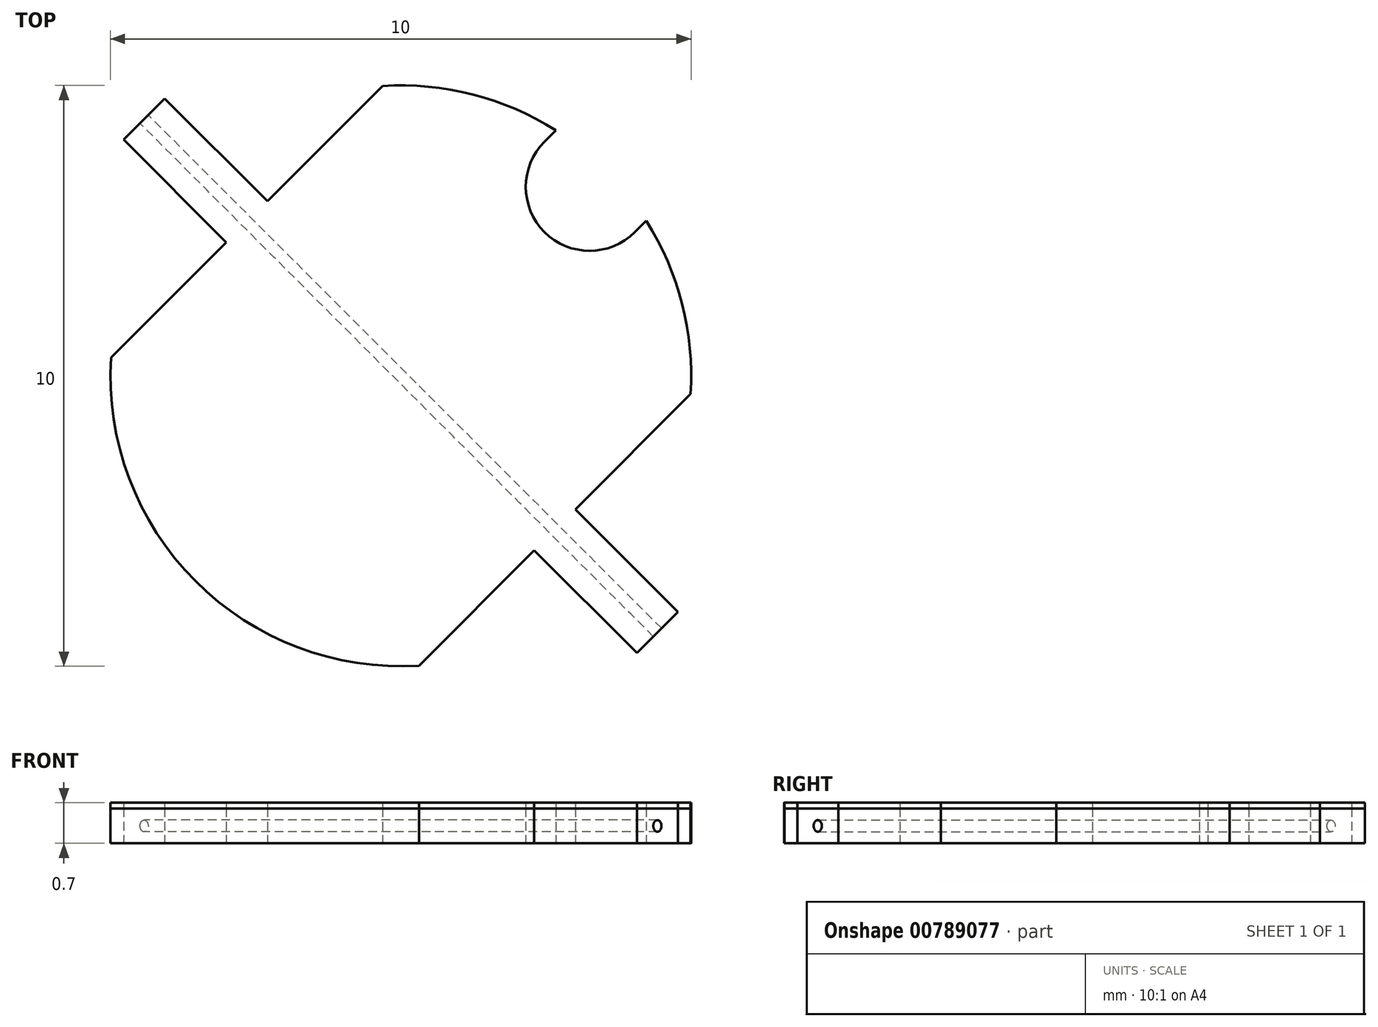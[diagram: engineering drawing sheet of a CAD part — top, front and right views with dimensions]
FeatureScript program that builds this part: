
annotation { "Feature Type Name" : "Feature", "Feature Type Description" : "" }
export const myFeature = defineFeature(function(context is Context, id is Id, definition is map)
    precondition{}
    {
        {
            var Q0;
            Q0=qCreatedBy(makeId("Top.planeOp"),FACE);
            var sketch = newSketch(context, id + "F0", { "sketchPlane" : qUnion([Q0])});
            skArc(sketch, "E0", {"start": v(-5, 0.31) * mm, "mid": v(-3.54, -3.54) * mm, "end": v(0.31, -5) * mm});
            skLineSegment(sketch, "E1.bottom", {"start": v(5, -5) * mm, "end": v(-5, -5) * mm, "construction": true});
            skLineSegment(sketch, "E1.top", {"start": v(5, 5) * mm, "end": v(-5, 5) * mm, "construction": true});
            skLineSegment(sketch, "E1.left", {"start": v(5, -5) * mm, "end": v(5, 5) * mm, "construction": true});
            skLineSegment(sketch, "E1.right", {"start": v(-5, -5) * mm, "end": v(-5, 5) * mm, "construction": true});
            skLineSegment(sketch, "E2", {"start": v(-4.07, 4.77) * mm, "end": v(-2.3, 3) * mm});
            skLineSegment(sketch, "E3", {"start": v(4.07, -4.77) * mm, "end": v(2.3, -3) * mm});
            skLineSegment(sketch, "E4", {"start": v(-4.77, 4.07) * mm, "end": v(-4.07, 4.77) * mm});
            skLineSegment(sketch, "E5.trimOffspring", {"start": v(3, -2.3) * mm, "end": v(4.77, -4.07) * mm});
            skLineSegment(sketch, "E6.trimOffspring", {"start": v(-3, 2.3) * mm, "end": v(-4.77, 4.07) * mm});
            skArc(sketch, "E7.trimOffspring", {"start": v(5, -0.31) * mm, "mid": v(4.84, 1.24) * mm, "end": v(4.23, 2.67) * mm});
            skLineSegment(sketch, "E8.bottom", {"start": v(-5, 5) * mm, "end": v(-0.3, 5) * mm, "construction": true});
            skLineSegment(sketch, "E8.top", {"start": v(-5, 0.3) * mm, "end": v(-0.3, 0.3) * mm, "construction": true});
            skLineSegment(sketch, "E8.left", {"start": v(-5, 5) * mm, "end": v(-5, 0.3) * mm, "construction": true});
            skLineSegment(sketch, "E8.right", {"start": v(-0.3, 5) * mm, "end": v(-0.3, 0.3) * mm, "construction": true});
            skLineSegment(sketch, "E9.bottom", {"start": v(5, -5) * mm, "end": v(0.3, -5) * mm, "construction": true});
            skLineSegment(sketch, "E9.top", {"start": v(5, -0.3) * mm, "end": v(0.3, -0.3) * mm, "construction": true});
            skLineSegment(sketch, "E9.left", {"start": v(5, -5) * mm, "end": v(5, -0.3) * mm, "construction": true});
            skLineSegment(sketch, "E9.right", {"start": v(0.3, -5) * mm, "end": v(0.3, -0.3) * mm, "construction": true});
            skLineSegment(sketch, "E10", {"start": v(-0.3, 5) * mm, "end": v(-2.3, 3) * mm});
            skLineSegment(sketch, "E11", {"start": v(5, -0.3) * mm, "end": v(3, -2.3) * mm});
            skLineSegment(sketch, "E12.trimOffspring", {"start": v(2.3, -3) * mm, "end": v(0.3, -5) * mm});
            skLineSegment(sketch, "E13.trimOffspring", {"start": v(-3, 2.3) * mm, "end": v(-5, 0.3) * mm});
            skLineSegment(sketch, "E14", {"start": v(-5, 3.84) * mm, "end": v(-3.84, 5) * mm, "construction": true});
            skLineSegment(sketch, "E15", {"start": v(-3.84, 5) * mm, "end": v(-0.44, 5) * mm, "construction": true});
            skLineSegment(sketch, "E16", {"start": v(-0.44, 5) * mm, "end": v(-5, 0.44) * mm, "construction": true});
            skLineSegment(sketch, "E17", {"start": v(-5, 0.44) * mm, "end": v(-5, 3.84) * mm, "construction": true});
            skLineSegment(sketch, "E18", {"start": v(-5, -5) * mm, "end": v(5, 5) * mm, "construction": true});
            skLineSegment(sketch, "E19.MirrorCS", {"start": v(5, -0.44) * mm, "end": v(0.44, -5) * mm, "construction": true});
            skLineSegment(sketch, "E20.MirrorCS", {"start": v(3.84, -5) * mm, "end": v(5, -3.84) * mm, "construction": true});
            skLineSegment(sketch, "E21", {"start": v(4.07, -4.77) * mm, "end": v(4.77, -4.07) * mm});
            skArc(sketch, "E22", {"start": v(2.47, 4.03) * mm, "mid": v(2.47, 2.47) * mm, "end": v(4.03, 2.47) * mm});
            skLineSegment(sketch, "E23", {"start": v(2.47, 4.03) * mm, "end": v(3.25, 3.25) * mm, "construction": true});
            skLineSegment(sketch, "E24", {"start": v(4.03, 2.47) * mm, "end": v(3.25, 3.25) * mm, "construction": true});
            skLineSegment(sketch, "E25", {"start": v(4.03, 2.47) * mm, "end": v(4.23, 2.67) * mm});
            skLineSegment(sketch, "E26", {"start": v(2.47, 4.03) * mm, "end": v(2.67, 4.23) * mm});
            skArc(sketch, "E27.trimOffspring", {"start": v(2.67, 4.23) * mm, "mid": v(1.24, 4.84) * mm, "end": v(-0.31, 5) * mm});
            skSolve(sketch);
        }
        {
            var Q0;
            Q0=makeQuery(id+"F0.imprint","IMPRINT",FACE,{"disambiguationData":[TD([[makeQuery(id+"F0.imprint","IMPRINT",EDGE,{"derivedFrom":sQuery(id+"F0.wireOp",EDGE,"E0")}),1.0]])]});
            extrude(context, id + "F1", {"entities" : qUnion([Q0]), "depth" : 0.6 * mm, "offsetDistance" : 25 * mm});
        }
        {
            var Q0;
            Q0=makeQuery(id+"F1.opExtrude","SWEPT_FACE",FACE,{"disambiguationData":[OSD([sQuery(id+"F0.wireOp",EDGE,"E4")])]});
            var sketch = newSketch(context, id + "F2", { "sketchPlane" : qUnion([Q0])});
            skLineSegment(sketch, "E28.bottom", {"start": v(-0.5, 0.6) * mm, "end": v(0.5, 0.6) * mm, "construction": true});
            skLineSegment(sketch, "E28.top", {"start": v(-0.5, 0) * mm, "end": v(0.5, 0) * mm, "construction": true});
            skLineSegment(sketch, "E28.left", {"start": v(-0.5, 0.6) * mm, "end": v(-0.5, 0) * mm, "construction": true});
            skLineSegment(sketch, "E28.right", {"start": v(0.5, 0.6) * mm, "end": v(0.5, 0) * mm, "construction": true});
            skLineSegment(sketch, "E29", {"start": v(-0.5, 0) * mm, "end": v(0.5, 0.6) * mm, "construction": true});
            skPoint(sketch, "E30", {"position": v(0, 0.3) * mm});
            skCircle(sketch, "E31", {"center": v(0, 0.3) * mm, "radius": 0.1 * mm});
            skSolve(sketch);
        }
        {
            var Q0;
            Q0 = qSketchRegion(id + "F2", true);
            extrude(context, id + "F3", {"entities" : qUnion([Q0]), "operationType" : NewBodyOperationType.REMOVE, "endBound" : BoundingType.UP_TO_NEXT, "oppositeDirection" : true, "depth" : 25 * mm, "offsetDistance" : 25 * mm});
        }
        {
            var Q0;
            Q0=makeQuery(id+"F1.opExtrude","CAP_FACE",FACE,{"disambiguationData":[OSD([sQuery(id+"F0.wireOp",EDGE,"E0"),sQuery(id+"F0.wireOp",EDGE,"E2"),sQuery(id+"F0.wireOp",EDGE,"E3"),sQuery(id+"F0.wireOp",EDGE,"E4"),sQuery(id+"F0.wireOp",EDGE,"E5.trimOffspring"),sQuery(id+"F0.wireOp",EDGE,"E6.trimOffspring"),sQuery(id+"F0.wireOp",EDGE,"E7.trimOffspring"),sQuery(id+"F0.wireOp",EDGE,"E10"),sQuery(id+"F0.wireOp",EDGE,"E11"),sQuery(id+"F0.wireOp",EDGE,"E12.trimOffspring"),sQuery(id+"F0.wireOp",EDGE,"E13.trimOffspring"),sQuery(id+"F0.wireOp",EDGE,"E21"),sQuery(id+"F0.wireOp",EDGE,"E22"),sQuery(id+"F0.wireOp",EDGE,"E25"),sQuery(id+"F0.wireOp",EDGE,"E26"),sQuery(id+"F0.wireOp",EDGE,"E27.trimOffspring")])],"isStart":false});
            var sketch = newSketch(context, id + "F4", { "sketchPlane" : qUnion([Q0])});
            skLineSegment(sketch, "E32.0.0", {"start": v(2.47, 4.03) * mm, "end": v(2.67, 4.23) * mm});
            skArc(sketch, "E32.0.1", {"start": v(2.67, 4.23) * mm, "mid": v(1.24, 4.84) * mm, "end": v(-0.31, 5) * mm});
            skLineSegment(sketch, "E32.0.2", {"start": v(-0.31, 5) * mm, "end": v(-2.3, 3) * mm});
            skLineSegment(sketch, "E32.0.3", {"start": v(-2.3, 3) * mm, "end": v(-4.07, 4.77) * mm});
            skLineSegment(sketch, "E32.0.4", {"start": v(-4.07, 4.77) * mm, "end": v(-4.77, 4.07) * mm});
            skLineSegment(sketch, "E32.0.5", {"start": v(-4.77, 4.07) * mm, "end": v(-3, 2.3) * mm});
            skLineSegment(sketch, "E32.0.6", {"start": v(-3, 2.3) * mm, "end": v(-5, 0.31) * mm});
            skArc(sketch, "E32.0.7", {"start": v(-5, 0.31) * mm, "mid": v(-3.54, -3.54) * mm, "end": v(0.31, -5) * mm});
            skLineSegment(sketch, "E32.0.8", {"start": v(0.31, -5) * mm, "end": v(2.3, -3) * mm});
            skLineSegment(sketch, "E32.0.9", {"start": v(2.3, -3) * mm, "end": v(4.07, -4.77) * mm});
            skLineSegment(sketch, "E32.0.10", {"start": v(4.07, -4.77) * mm, "end": v(4.77, -4.07) * mm});
            skLineSegment(sketch, "E32.0.11", {"start": v(4.77, -4.07) * mm, "end": v(3, -2.3) * mm});
            skLineSegment(sketch, "E32.0.12", {"start": v(3, -2.3) * mm, "end": v(5, -0.31) * mm});
            skArc(sketch, "E32.0.13", {"start": v(5, -0.31) * mm, "mid": v(4.84, 1.24) * mm, "end": v(4.23, 2.67) * mm});
            skLineSegment(sketch, "E32.0.14", {"start": v(4.23, 2.67) * mm, "end": v(4.03, 2.47) * mm});
            skArc(sketch, "E32.0.15", {"start": v(4.03, 2.47) * mm, "mid": v(2.47, 2.47) * mm, "end": v(2.47, 4.03) * mm});
            skSolve(sketch);
        }
        {
            var Q0;
            Q0 = qSketchRegion(id + "F4", true);
            extrude(context, id + "F5", {"entities" : qUnion([Q0]), "depth" : 0.1 * mm, "offsetDistance" : 25 * mm});
        }
    });
